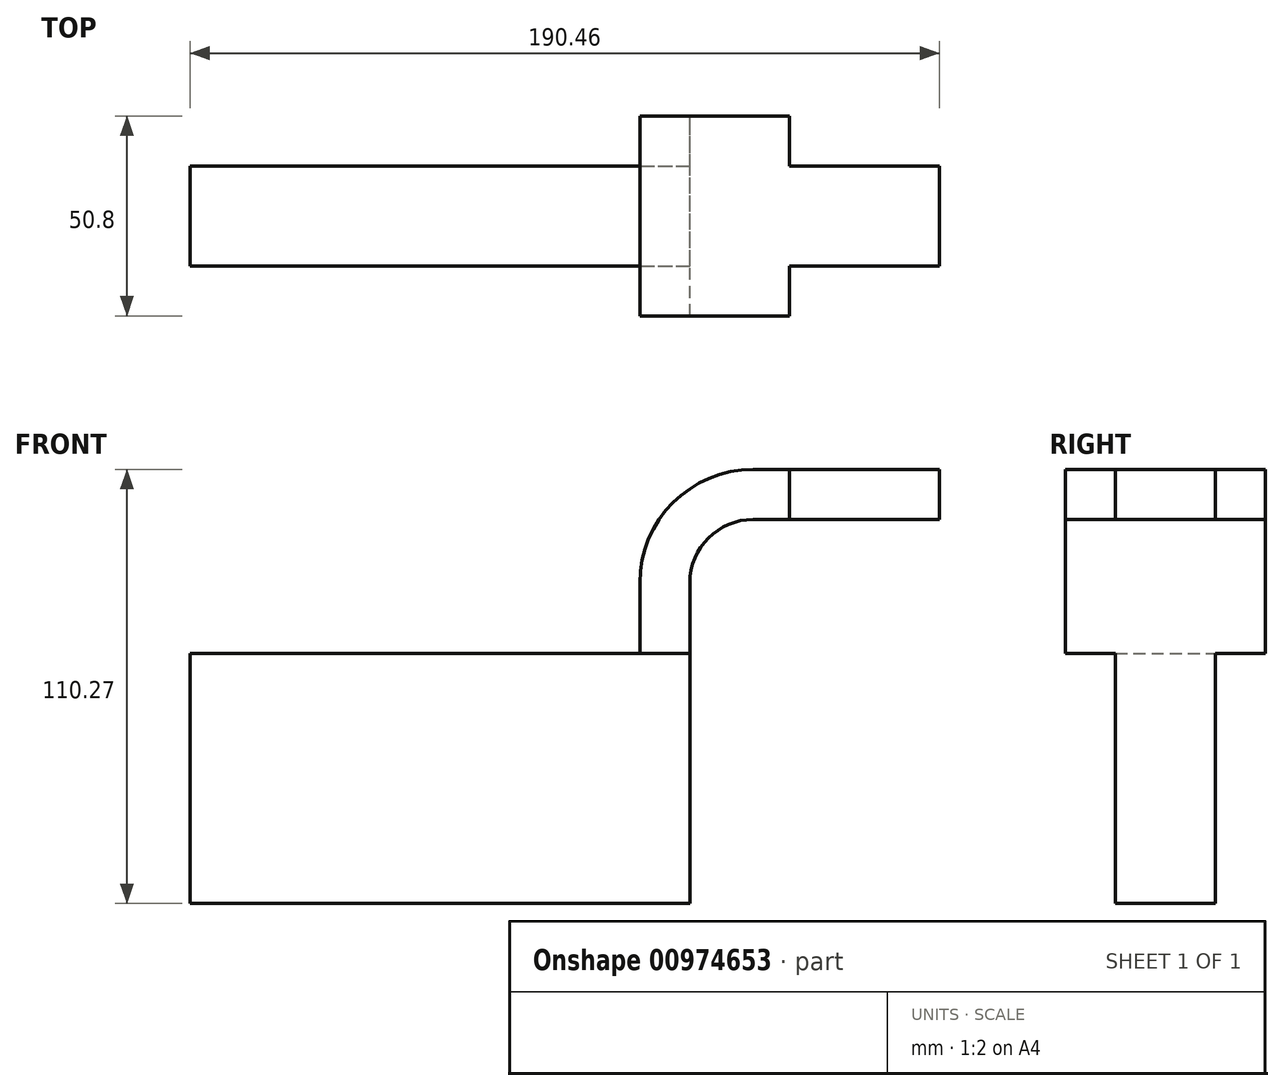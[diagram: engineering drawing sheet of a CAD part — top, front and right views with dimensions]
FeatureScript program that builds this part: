
annotation { "Feature Type Name" : "Feature", "Feature Type Description" : "" }
export const myFeature = defineFeature(function(context is Context, id is Id, definition is map)
    precondition{}
    {
        {
            var Q0;
            Q0=qCreatedBy(makeId("Front.planeOp"),FACE);
            var sketch = newSketch(context, id + "F0", { "sketchPlane" : qUnion([Q0])});
            skLineSegment(sketch, "E0.bottom", {"start": v(-63.5, -31.75) * mm, "end": v(63.5, -31.75) * mm});
            skLineSegment(sketch, "E0.top", {"start": v(-63.5, 31.75) * mm, "end": v(63.5, 31.75) * mm});
            skLineSegment(sketch, "E0.left", {"start": v(-63.5, -31.75) * mm, "end": v(-63.5, 31.75) * mm});
            skLineSegment(sketch, "E0.right", {"start": v(63.5, -31.75) * mm, "end": v(63.5, 31.75) * mm});
            skPoint(sketch, "E0.middle", {"position": v(0, 0) * mm});
            skLineSegment(sketch, "E1.bottom", {"start": v(126.96, 65.82) * mm, "end": v(88.86, 65.82) * mm});
            skLineSegment(sketch, "E1.top", {"start": v(126.96, 78.52) * mm, "end": v(88.86, 78.52) * mm});
            skLineSegment(sketch, "E1.left", {"start": v(126.96, 65.82) * mm, "end": v(126.96, 78.52) * mm});
            skLineSegment(sketch, "E1.right", {"start": v(88.86, 65.82) * mm, "end": v(88.86, 78.52) * mm});
            skPoint(sketch, "E1.middle", {"position": v(107.91, 72.17) * mm});
            skLineSegment(sketch, "E2", {"start": v(63.5, 31.75) * mm, "end": v(63.5, 49.72) * mm});
            skArc(sketch, "E3", {"start": v(63.5, 49.72) * mm, "mid": v(68.21, 61.1) * mm, "end": v(79.6, 65.82) * mm});
            skLineSegment(sketch, "E4", {"start": v(79.6, 65.82) * mm, "end": v(88.86, 65.82) * mm});
            skLineSegment(sketch, "E5.0", {"start": v(79.6, 78.52) * mm, "end": v(88.86, 78.52) * mm});
            skArc(sketch, "E5.1", {"start": v(50.8, 49.72) * mm, "mid": v(59.23, 70.08) * mm, "end": v(79.6, 78.52) * mm});
            skLineSegment(sketch, "E5.2", {"start": v(50.8, 31.75) * mm, "end": v(50.8, 49.72) * mm});
            skSolve(sketch);
        }
        {
            var Q0;
            Q0=makeQuery(id+"F0.imprint","IMPRINT",FACE,{"disambiguationData":[TD([[makeQuery(id+"F0.imprint","IMPRINT",EDGE,{"derivedFrom":sQuery(id+"F0.wireOp",EDGE,"E0.bottom")}),1.0]])]});
            extrude(context, id + "F1", {"entities" : qUnion([Q0]), "endBound" : BoundingType.SYMMETRIC, "depth" : 25.4 * mm, "offsetDistance" : 25.4 * mm});
        }
        {
            var Q0;
            Q0=makeQuery(id+"F0.imprint","IMPRINT",FACE,{"disambiguationData":[TD([[makeQuery(id+"F0.imprint","IMPRINT",EDGE,{"derivedFrom":sQuery(id+"F0.wireOp",EDGE,"E1.right")}),1.0]])]});
            extrude(context, id + "F2", {"entities" : qUnion([Q0]), "operationType" : NewBodyOperationType.ADD, "endBound" : BoundingType.SYMMETRIC, "depth" : 50.8 * mm, "offsetDistance" : 25.4 * mm});
        }
        {
            var Q0;
            Q0=makeQuery(id+"F0.imprint","IMPRINT",FACE,{"disambiguationData":[TD([[makeQuery(id+"F0.imprint","IMPRINT",EDGE,{"derivedFrom":sQuery(id+"F0.wireOp",EDGE,"E1.bottom")}),-1.0]])]});
            extrude(context, id + "F3", {"entities" : qUnion([Q0]), "operationType" : NewBodyOperationType.ADD, "endBound" : BoundingType.SYMMETRIC, "depth" : 25.4 * mm, "offsetDistance" : 25.4 * mm});
        }
    });
